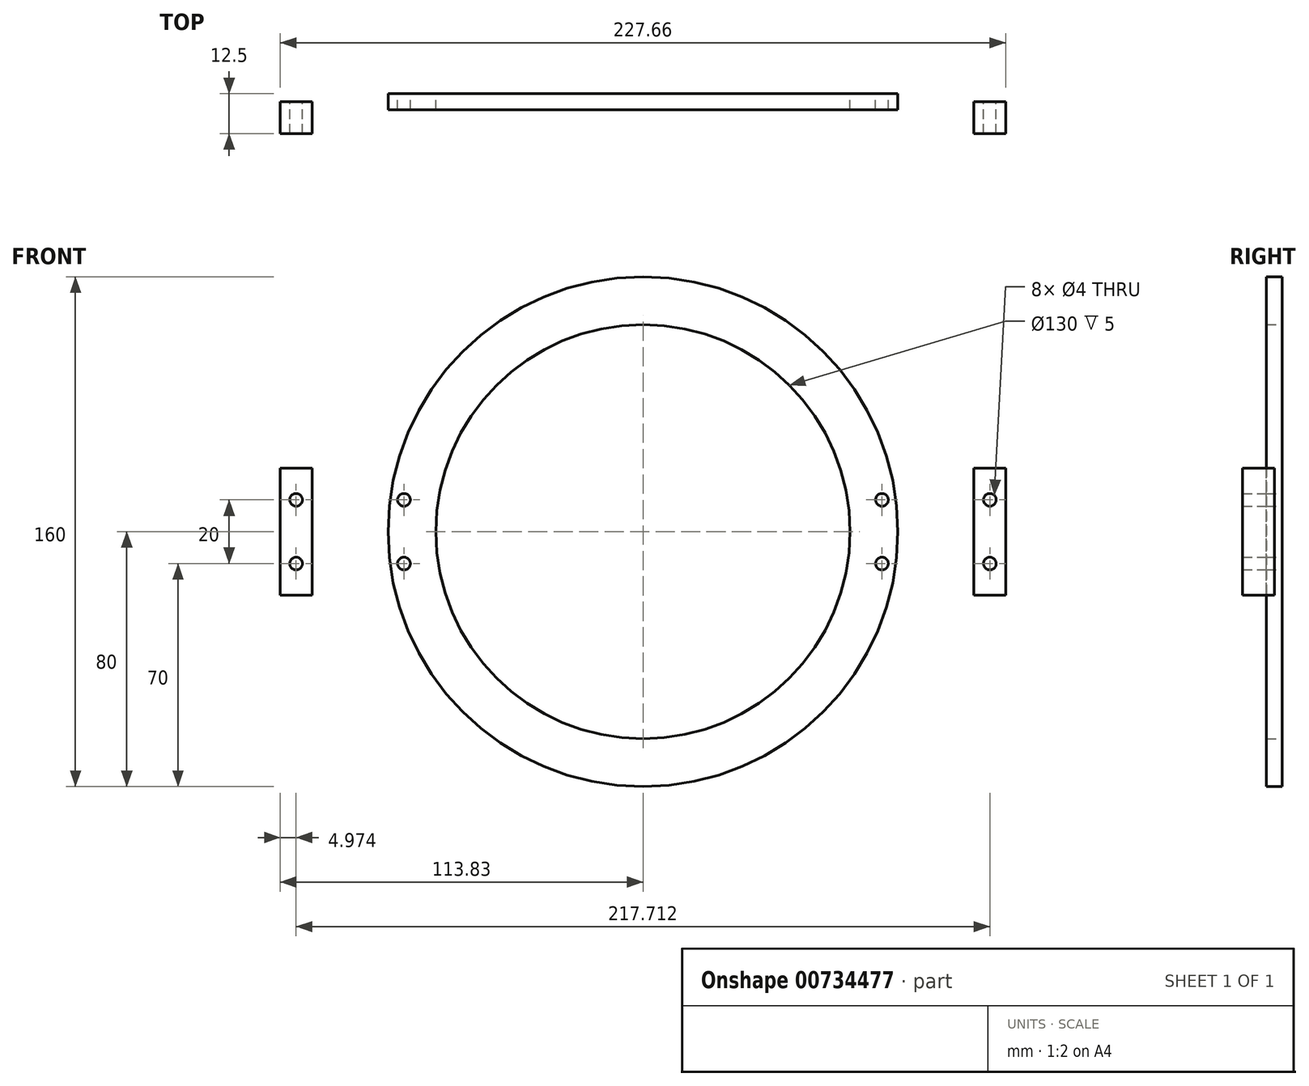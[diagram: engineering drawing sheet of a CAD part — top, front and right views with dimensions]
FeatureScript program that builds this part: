
annotation { "Feature Type Name" : "Feature", "Feature Type Description" : "" }
export const myFeature = defineFeature(function(context is Context, id is Id, definition is map)
    precondition{}
    {
        {
            var Q0;
            Q0=qCreatedBy(makeId("Front.planeOp"),FACE);
            var sketch = newSketch(context, id + "F0", { "sketchPlane" : qUnion([Q0])});
            skCircle(sketch, "E0", {"center": v(0, 0) * mm, "radius": 65 * mm});
            skCircle(sketch, "E1", {"center": v(0, 0) * mm, "radius": 80 * mm});
            skCircle(sketch, "E2", {"center": v(75, 10) * mm, "radius": 2 * mm});
            skCircle(sketch, "E3.MirrorC", {"center": v(75, -10) * mm, "radius": 2 * mm});
            skCircle(sketch, "E4.MirrorC", {"center": v(-75, 10) * mm, "radius": 2 * mm});
            skCircle(sketch, "E5.MirrorC", {"center": v(-75, -10) * mm, "radius": 2 * mm});
            skSolve(sketch);
        }
        {
            var Q0;
            Q0 = qSketchRegion(id + "F0", true);
            extrude(context, id + "F1", {"entities" : qUnion([Q0]), "depth" : 5 * mm, "offsetDistance" : 25 * mm, "symmetric" : true});
        }
        {
            var Q0;
            Q0=qCreatedBy(makeId("Front.planeOp"),FACE);
            var sketch = newSketch(context, id + "F2", { "sketchPlane" : qUnion([Q0])});
            skLineSegment(sketch, "E6.bottom", {"start": v(-113.83, 20) * mm, "end": v(-103.83, 20) * mm});
            skLineSegment(sketch, "E6.top", {"start": v(-113.83, -20) * mm, "end": v(-103.83, -20) * mm});
            skLineSegment(sketch, "E6.left", {"start": v(-113.83, 20) * mm, "end": v(-113.83, -20) * mm});
            skLineSegment(sketch, "E6.right", {"start": v(-103.83, 20) * mm, "end": v(-103.83, -20) * mm});
            skLineSegment(sketch, "E7", {"start": v(-134.02, 0) * mm, "end": v(-90, 0) * mm, "construction": true});
            skPoint(sketch, "E7.endSnap0", {"position": v(-103.83, 0) * mm});
            skCircle(sketch, "E8", {"center": v(-108.86, 10) * mm, "radius": 2 * mm});
            skCircle(sketch, "E9.MirrorC", {"center": v(-108.86, -10) * mm, "radius": 2 * mm});
            skLineSegment(sketch, "E10.MirrorCS", {"start": v(103.83, 20) * mm, "end": v(103.83, -20) * mm});
            skLineSegment(sketch, "E11.MirrorCS", {"start": v(113.83, 20) * mm, "end": v(113.83, -20) * mm});
            skLineSegment(sketch, "E12.MirrorCS", {"start": v(113.83, 20) * mm, "end": v(103.83, 20) * mm});
            skCircle(sketch, "E13.MirrorC", {"center": v(108.86, 10) * mm, "radius": 2 * mm});
            skPoint(sketch, "E14.MirrorP", {"position": v(103.83, 0) * mm});
            skCircle(sketch, "E15.MirrorC", {"center": v(108.86, -10) * mm, "radius": 2 * mm});
            skLineSegment(sketch, "E16.MirrorCS", {"start": v(113.83, -20) * mm, "end": v(103.83, -20) * mm});
            skSolve(sketch);
        }
        {
            var Q0;
            Q0 = qSketchRegion(id + "F2", true);
            extrude(context, id + "F3", {"entities" : qUnion([Q0]), "depth" : 10 * mm, "offsetDistance" : 25 * mm});
        }
    });
